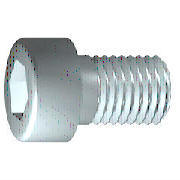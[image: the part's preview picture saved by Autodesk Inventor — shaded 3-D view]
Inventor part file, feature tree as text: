
AUTODESK INVENTOR PART (.ipt)
format: ipt  version: 2020 (Build 240168000, 168)  size: 194,048 bytes
history: native  units: mm (DEFAULTED — no unit token found)
features: sketch x2, other x1, extrude x1, plane x1, fillet x1
ambient origin geometry x7: Origin, YZ Plane, XY Plane, X Axis, Y Axis, Z Axis, Center Point
bodies: Solid1 (feature_tree)
feature tree (6):
  other  "Bryła"
  extrude  "Szczelina"  Depth=12.5mm
  plane  "Work Plane1"
  fillet  "Fillet2"  Radius=0.306825mm
  sketch  "Szkic1"
  sketch  "Szkic2"
